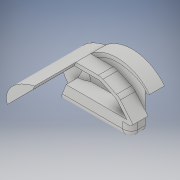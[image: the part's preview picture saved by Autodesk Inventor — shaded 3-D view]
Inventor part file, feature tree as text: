
AUTODESK INVENTOR PART (.ipt)
format: ipt  version: 2017 (Build 210142000, 142)  size: 559,616 bytes
history: native  units: mm
features: sketch x25, extrude x21, plane x7, fillet x4, other x3, revolve x1, boolean_combine x1
ambient origin geometry x8: Origin, YZ Plane, XZ Plane, XY Plane, X Axis, Y Axis, Z Axis, Center Point
bodies: Solid1 (feature_tree), Solid2 (feature_tree)
feature tree (62):
  extrude  "Extrusion1"  Depth=35.0mm
  plane  "Work Plane1"
  extrude  "Extrusion2"  Depth=33.005006mm
  other  "Bend Part1"
  other  "Bend Part2"
  extrude  "Extrusion3"  Depth=32.454mm
  plane  "Work Plane2"
  extrude  "Extrusion4"  Depth=20.0mm
  other  "Bend Part3"
  extrude  "Extrusion5"  Depth=30.0mm
  revolve  "Revolution1"  [1 undecoded]
  plane  "Work Plane3"
  extrude  "Extrusion6"  Depth=20.0mm
  boolean_combine  "Combine1"
  plane  "Work Plane4"
  extrude  "Extrusion7"  TaperAngle=90.0deg  [1 undecoded]
  extrude  "Extrusion8"  Depth=20.0mm
  extrude  "Extrusion9"  Depth=50.0mm TaperAngle=135.0deg
  extrude  "Extrusion10"  Depth=35.0mm
  plane  "Work Plane5"
  extrude  "Extrusion11"  Depth=60.0mm
  extrude  "Extrusion12"  Depth=20.0mm
  plane  "Work Plane6"
  extrude  "Extrusion13"  [1 undecoded]
  extrude  "Extrusion14"  Depth=20.0mm TaperAngle=0.0deg
  plane  "Work Plane7"
  extrude  "Extrusion15"  Depth=20.0mm TaperAngle=0.0deg
  extrude  "Extrusion16"  Depth=15.219936mm
  extrude  "Extrusion17"  Depth=20.0mm
  fillet  "Fillet1"  Radius=20.0mm
  extrude  "Extrusion18"  Depth=20.0mm
  fillet  "Fillet2"  Radius=43.193283mm
  fillet  "Fillet3"  Radius=60.0mm
  fillet  "Fillet4"  Radius=60.5mm
  extrude  "Extrusion19"  Depth=25.287025mm
  extrude  "Extrusion20"  Depth=2.439mm TaperAngle=0.0deg
  extrude  "Extrusion21"  Depth=0.980484mm
  sketch  "Sketch1"  dims[d0=60.0mm d1=35.0mm]
  sketch  "Sketch2"  dims[d2=60.0mm d3=33.005006mm]
  sketch  "Sketch3"  dims[d4=75.0mm d5=0.0mm d6=32.454mm]
  sketch  "Sketch4"  dims[d7=85.0mm d8=20.0mm]
  sketch  "Sketch5"  dims[d9=5.0mm d10=0.0mm d11=30.0mm]
  sketch  "Sketch6"  dims[d12=55.0mm d13=10.0mm d14=4.363323mm]
  sketch  "Sketch7"  dims[d15=20.0mm d16=10.0mm d17=4.363323mm]
  sketch  "Sketch8"  dims[d18=20.0mm d19=0.0mm d20=90.0deg]
  sketch  "Sketch9"  dims[d21=20.0mm d22=80.0mm]
  sketch  "Sketch10"  dims[d23=5.0mm d24=0.0mm d25=50.0mm d26=135.0deg]
  sketch  "Sketch11"  dims[d27=60.0mm d28=35.0mm]
  sketch  "Sketch12"  dims[d29=35.0mm d30=60.0mm]
  sketch  "Sketch13"  dims[d31=20.0mm d32=0.0mm d33=60.0mm]
  sketch  "Sketch14"  dims[d34=270.0deg d35=-4.697mm]
  sketch  "Sketch15"  dims[d36=20.0mm d37=30.0mm d38=0.0mm]
  sketch  "Sketch16"  dims[d39=-20.0mm d40=20.0mm d41=0.0mm]
  sketch  "Sketch17"  dims[d42=35.67mm d43=15.219936mm]
  sketch  "Sketch18"  dims[d44=35.67mm d45=15.155142mm d46=20.0mm d47=0.0mm]
  sketch  "Sketch19"  dims[d48=20.0mm d49=0.0mm d50=100.334153mm d51=43.193283mm d52=60.0mm d53=0.0mm d54=60.5mm]
  sketch  "Sketch20"  dims[d55=14.497104mm d56=25.287025mm]
  sketch  "Sketch21"  dims[d57=104.0mm d58=0.0mm d59=2.439mm d60=0.0mm]
  sketch  "Sketch22"  dims[d61=-31.25mm d62=0.980484mm]
  sketch  "Sketch23"  dims[d63=1.164325mm]
  sketch  "Sketch24"  dims[d64=2.246206mm]
  sketch  "Sketch25"  dims[d65=25.536883mm d66=100.0mm d67=0.0mm d68=0.0mm d69=5.0mm d70=0.0mm d71=50.209mm d72=95.197mm d73=0.0mm d74=95.197mm d75=0.0mm d76=60.0mm d77=60.0mm d78=20.0mm d79=18.461mm d80=116.447mm d81=0.0mm d82=10.0mm d83=8.797686mm d84=116.447mm d85=0.0mm d86=10.0mm d87=9.0mm d88=10.0mm d89=60.197145mm d90=34.482005mm d91=20.0mm d92=3.0mm d93=20.0mm d94=90.0deg d95=55.512917mm d96=23.386841mm d97=11.976391mm d98=75.0mm d99=0.0mm d100=3.0mm d101=20.0mm d102=75.0mm d103=0.0mm d104=14.0mm d105=2.0mm d106=75.0mm d107=0.0mm]
note: 3 required parameter values undecoded (feature->parameter linkage not recoverable at this tier; creation-order binding heuristic only, values carry confidence <= 0.55)